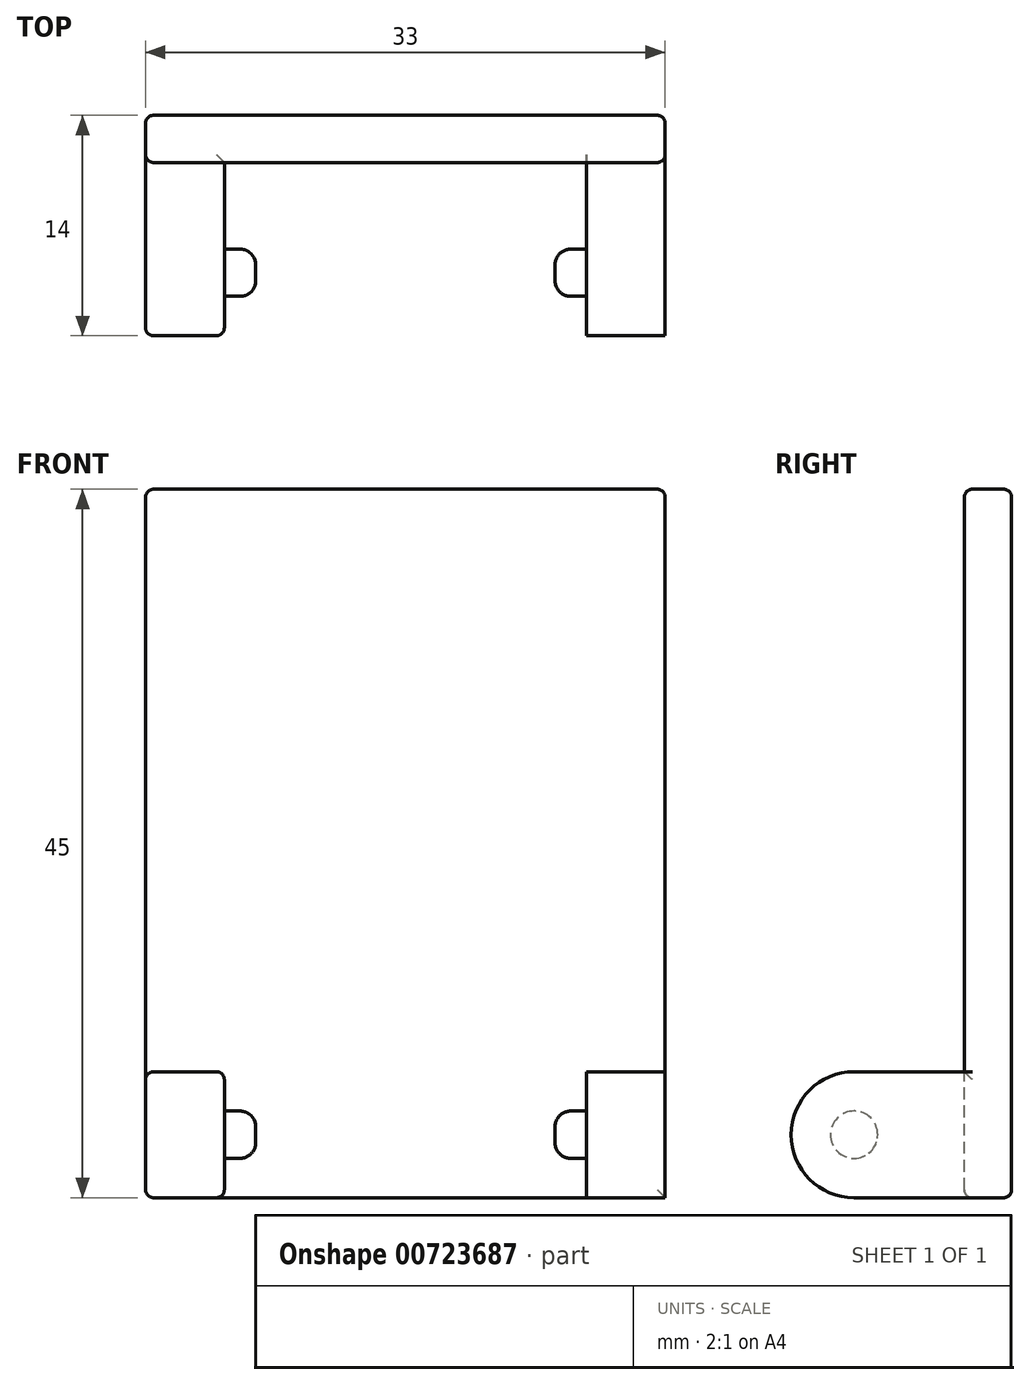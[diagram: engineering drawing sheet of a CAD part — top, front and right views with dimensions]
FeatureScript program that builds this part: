
annotation { "Feature Type Name" : "Feature", "Feature Type Description" : "" }
export const myFeature = defineFeature(function(context is Context, id is Id, definition is map)
    precondition{}
    {
        {
            var Q0;
            Q0=qCreatedBy(makeId("Front.planeOp"),FACE);
            var sketch = newSketch(context, id + "F0", { "sketchPlane" : qUnion([Q0])});
            skLineSegment(sketch, "E0.bottom", {"start": v(0, 0) * mm, "end": v(33, 0) * mm});
            skLineSegment(sketch, "E0.top", {"start": v(0, 45) * mm, "end": v(33, 45) * mm});
            skLineSegment(sketch, "E0.left", {"start": v(0, 0) * mm, "end": v(0, 45) * mm});
            skLineSegment(sketch, "E0.right", {"start": v(33, 0) * mm, "end": v(33, 45) * mm});
            skSolve(sketch);
        }
        {
            var Q0;
            Q0=makeQuery(id+"F0.imprint","IMPRINT",FACE,{"disambiguationData":[TD([[makeQuery(id+"F0.imprint","IMPRINT",EDGE,{"derivedFrom":sQuery(id+"F0.wireOp",EDGE,"E0.bottom")}),1.0]])]});
            extrude(context, id + "F1", {"entities" : qUnion([Q0]), "oppositeDirection" : true, "depth" : 3 * mm, "offsetDistance" : 25 * mm});
        }
        {
            var Q0;
            Q0=makeQuery(id+"F0.imprint","IMPRINT",FACE,{"disambiguationData":[TD([[makeQuery(id+"F0.imprint","IMPRINT",EDGE,{"derivedFrom":sQuery(id+"F0.wireOp",EDGE,"E0.bottom")}),1.0]])]});
            var sketch = newSketch(context, id + "F2", { "sketchPlane" : qUnion([Q0])});
            skLineSegment(sketch, "E1.bottom", {"start": v(0, 0) * mm, "end": v(5, 0) * mm});
            skLineSegment(sketch, "E1.top", {"start": v(0, 8) * mm, "end": v(5, 8) * mm});
            skLineSegment(sketch, "E1.left", {"start": v(0, 0) * mm, "end": v(0, 8) * mm});
            skLineSegment(sketch, "E1.right", {"start": v(5, 0) * mm, "end": v(5, 8) * mm});
            skLineSegment(sketch, "E2.bottom", {"start": v(33, 0) * mm, "end": v(28, 0) * mm});
            skLineSegment(sketch, "E2.top", {"start": v(33, 8) * mm, "end": v(28, 8) * mm});
            skLineSegment(sketch, "E2.left", {"start": v(33, 0) * mm, "end": v(33, 8) * mm});
            skLineSegment(sketch, "E2.right", {"start": v(28, 0) * mm, "end": v(28, 8) * mm});
            skSolve(sketch);
        }
        {
            var Q0;
            Q0 = qSketchRegion(id + "F2", true);
            extrude(context, id + "F3", {"entities" : qUnion([Q0]), "operationType" : NewBodyOperationType.ADD, "depth" : 11 * mm, "offsetDistance" : 25 * mm});
        }
        {
            var Q0;
            Q0=makeQuery(id+"F3.opExtrude","SWEPT_FACE",FACE,{"disambiguationData":[OSD([sQuery(id+"F2.wireOp",EDGE,"E1.right")])]});
            var sketch = newSketch(context, id + "F4", { "sketchPlane" : qUnion([Q0])});
            skCircle(sketch, "E3", {"center": v(-7, 4) * mm, "radius": 1.5 * mm});
            skSolve(sketch);
        }
        {
            var Q0;
            Q0=makeQuery(id+"F4.imprint","IMPRINT",FACE,{"disambiguationData":[TD([[makeQuery(id+"F4.imprint","IMPRINT",EDGE,{"derivedFrom":sQuery(id+"F4.wireOp",EDGE,"E3")}),1.0]])]});
            extrude(context, id + "F5", {"entities" : qUnion([Q0]), "operationType" : NewBodyOperationType.ADD, "depth" : 2 * mm, "offsetDistance" : 25 * mm});
        }
        {
            var Q0;
            Q0=makeQuery(id+"F5.opExtrude","CAP_EDGE",EDGE,{"disambiguationData":[OSD([sQuery(id+"F4.wireOp",EDGE,"E3")])],"isStart":false});
            fillet(context, id + "F6", {"entities" : qUnion([Q0]), "radius" : 1 * mm, "tangentPropagation" : true, "allowEdgeOverflow" : false});
        }
        {
            var Q0;
            Q0=makeQuery(id+"F3.opExtrude","SWEPT_FACE",FACE,{"disambiguationData":[OSD([sQuery(id+"F2.wireOp",EDGE,"E2.right")])]});
            var sketch = newSketch(context, id + "F7", { "sketchPlane" : qUnion([Q0])});
            skCircle(sketch, "E4", {"center": v(7, 4) * mm, "radius": 1.5 * mm});
            skSolve(sketch);
        }
        {
            var Q0;
            Q0=makeQuery(id+"F7.imprint","IMPRINT",FACE,{"disambiguationData":[TD([[makeQuery(id+"F7.imprint","IMPRINT",EDGE,{"derivedFrom":sQuery(id+"F7.wireOp",EDGE,"E4")}),1.0]])]});
            extrude(context, id + "F8", {"entities" : qUnion([Q0]), "operationType" : NewBodyOperationType.ADD, "depth" : 2 * mm, "offsetDistance" : 25 * mm});
        }
        {
            var Q0;
            Q0=makeQuery(id+"F8.opExtrude","CAP_EDGE",EDGE,{"disambiguationData":[OSD([sQuery(id+"F7.wireOp",EDGE,"E4")])],"isStart":false});
            fillet(context, id + "F9", {"entities" : qUnion([Q0]), "radius" : 1 * mm, "tangentPropagation" : true, "allowEdgeOverflow" : false});
        }
        {
            var Q0;
            Q0=makeQuery(id+"F3.opExtrude","CAP_EDGE",EDGE,{"disambiguationData":[OSD([sQuery(id+"F2.wireOp",EDGE,"E1.top")])],"isStart":false});
            var Q1;
            Q1=makeQuery(id+"F3.opExtrude","CAP_EDGE",EDGE,{"disambiguationData":[OSD([sQuery(id+"F2.wireOp",EDGE,"E1.bottom")])],"isStart":false});
            var Q2;
            Q2=makeQuery(id+"F3.opExtrude","CAP_EDGE",EDGE,{"disambiguationData":[OSD([sQuery(id+"F2.wireOp",EDGE,"E2.top")])],"isStart":false});
            var Q3;
            Q3=makeQuery(id+"F3.opExtrude","CAP_EDGE",EDGE,{"disambiguationData":[OSD([sQuery(id+"F2.wireOp",EDGE,"E2.bottom")])],"isStart":false});
            fillet(context, id + "F10", {"entities" : qUnion([Q0, Q1, Q2, Q3]), "radius" : 4 * mm, "tangentPropagation" : true, "allowEdgeOverflow" : false});
        }
        {
            var Q0;
            Q0=makeQuery(id+"F1.opExtrude","CAP_EDGE",EDGE,{"disambiguationData":[OSD([sQuery(id+"F0.wireOp",EDGE,"E0.left")])],"isStart":true});
            var Q1;
            Q1=makeQuery(id+"F1.opExtrude","CAP_EDGE",EDGE,{"disambiguationData":[OSD([sQuery(id+"F0.wireOp",EDGE,"E0.top")])],"isStart":true});
            var Q2;
            Q2=makeQuery(id+"F1.opExtrude","CAP_EDGE",EDGE,{"disambiguationData":[OSD([sQuery(id+"F0.wireOp",EDGE,"E0.right")])],"isStart":true});
            var Q3;
            Q3=makeQuery(id+"F1.opExtrude","SWEPT_EDGE",EDGE,{"disambiguationData":[OSD([sQuery(id+"F0.wireOp",EDGE,"E0.top"),sQuery(id+"F0.wireOp",EDGE,"E0.right")])]});
            var Q4;
            Q4=makeQuery(id+"F1.opExtrude","CAP_EDGE",EDGE,{"disambiguationData":[OSD([sQuery(id+"F0.wireOp",EDGE,"E0.right")])],"isStart":false});
            var Q5;
            Q5=makeQuery(id+"F1.opExtrude","SWEPT_EDGE",EDGE,{"disambiguationData":[OSD([sQuery(id+"F0.wireOp",EDGE,"E0.top"),sQuery(id+"F0.wireOp",EDGE,"E0.left")])]});
            var Q6;
            Q6=makeQuery(id+"F1.opExtrude","CAP_EDGE",EDGE,{"disambiguationData":[OSD([sQuery(id+"F0.wireOp",EDGE,"E0.top")])],"isStart":false});
            var Q7;
            Q7=makeQuery(id+"F1.opExtrude","CAP_EDGE",EDGE,{"disambiguationData":[OSD([sQuery(id+"F0.wireOp",EDGE,"E0.left")])],"isStart":false});
            var Q8;
            Q8=makeQuery(id+"F1.opExtrude","CAP_EDGE",EDGE,{"disambiguationData":[OSD([sQuery(id+"F0.wireOp",EDGE,"E0.bottom")])],"isStart":true});
            var Q9;
            Q9=makeQuery(id+"F3.opExtrude","CAP_EDGE",EDGE,{"disambiguationData":[OSD([sQuery(id+"F2.wireOp",EDGE,"E2.right")])],"isStart":true});
            var Q10;
            Q10=makeQuery(id+"F3.boolean.opBoolean","MERGE",EDGE,{"derivedFrom":[makeQuery(id+"F1.opExtrude","SWEPT_EDGE",EDGE,{"disambiguationData":[OSD([sQuery(id+"F0.wireOp",EDGE,"E0.bottom"),sQuery(id+"F0.wireOp",EDGE,"E0.left")])]}),makeQuery(id+"F3.opExtrude","SWEPT_EDGE",EDGE,{"disambiguationData":[OSD([sQuery(id+"F2.wireOp",EDGE,"E1.bottom"),sQuery(id+"F2.wireOp",EDGE,"E1.left")])]})]});
            var Q11;
            Q11=makeQuery(id+"F10.opFillet","BLEND_EDGE",EDGE,{"blendedFrom":[makeQuery(id+"F3.opExtrude","CAP_EDGE",EDGE,{"disambiguationData":[OSD([sQuery(id+"F2.wireOp",EDGE,"E1.bottom")])],"isStart":false}),makeQuery(id+"F3.boolean.opBoolean","MERGE",FACE,{"derivedFrom":[makeQuery(id+"F1.opExtrude","SWEPT_FACE",FACE,{"disambiguationData":[OSD([sQuery(id+"F0.wireOp",EDGE,"E0.left")])]}),makeQuery(id+"F3.opExtrude","SWEPT_FACE",FACE,{"disambiguationData":[OSD([sQuery(id+"F2.wireOp",EDGE,"E1.left")])]})]})],"blendedInto":[makeQuery(id+"F3.boolean.opBoolean","MERGE",FACE,{"derivedFrom":[makeQuery(id+"F1.opExtrude","SWEPT_FACE",FACE,{"disambiguationData":[OSD([sQuery(id+"F0.wireOp",EDGE,"E0.left")])]}),makeQuery(id+"F3.opExtrude","SWEPT_FACE",FACE,{"disambiguationData":[OSD([sQuery(id+"F2.wireOp",EDGE,"E1.left")])]})]})]});
            var Q12;
            Q12=makeQuery(id+"F3.opExtrude","SWEPT_EDGE",EDGE,{"disambiguationData":[OSD([sQuery(id+"F0.wireOp",EDGE,"E0.left"),sQuery(id+"F2.wireOp",EDGE,"E1.top"),sQuery(id+"F2.wireOp",EDGE,"E1.left")])]});
            var Q13;
            Q13=makeQuery(id+"F10.opFillet","BLEND_EDGE",EDGE,{"blendedFrom":[makeQuery(id+"F3.opExtrude","CAP_EDGE",EDGE,{"disambiguationData":[OSD([sQuery(id+"F2.wireOp",EDGE,"E1.bottom")])],"isStart":false}),makeQuery(id+"F3.opExtrude","SWEPT_FACE",FACE,{"disambiguationData":[OSD([sQuery(id+"F2.wireOp",EDGE,"E1.right")])]})],"blendedInto":[makeQuery(id+"F3.opExtrude","SWEPT_FACE",FACE,{"disambiguationData":[OSD([sQuery(id+"F2.wireOp",EDGE,"E1.right")])]})]});
            var Q14;
            Q14=makeQuery(id+"F3.opExtrude","SWEPT_EDGE",EDGE,{"disambiguationData":[OSD([sQuery(id+"F0.wireOp",EDGE,"E0.bottom"),sQuery(id+"F2.wireOp",EDGE,"E1.bottom"),sQuery(id+"F2.wireOp",EDGE,"E1.right")])]});
            var Q15;
            Q15=makeQuery(id+"F1.opExtrude","CAP_EDGE",EDGE,{"disambiguationData":[OSD([sQuery(id+"F0.wireOp",EDGE,"E0.bottom")])],"isStart":false});
            var Q16;
            Q16=makeQuery(id+"F3.opExtrude","SWEPT_EDGE",EDGE,{"disambiguationData":[OSD([sQuery(id+"F2.wireOp",EDGE,"E1.top"),sQuery(id+"F2.wireOp",EDGE,"E1.right")])]});
            var Q17;
            Q17=makeQuery(id+"F3.opExtrude","CAP_EDGE",EDGE,{"disambiguationData":[OSD([sQuery(id+"F2.wireOp",EDGE,"E1.top")])],"isStart":true});
            fillet(context, id + "F11", {"entities" : qUnion([Q0, Q1, Q2, Q3, Q4, Q5, Q6, Q7, Q8, Q9, Q10, Q11, Q12, Q13, Q14, Q15, Q16, Q17]), "radius" : 0.5 * mm, "tangentPropagation" : true, "allowEdgeOverflow" : false});
        }
    });
